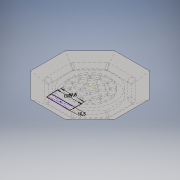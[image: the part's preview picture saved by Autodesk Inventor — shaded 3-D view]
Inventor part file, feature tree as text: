
AUTODESK INVENTOR PART (.ipt)
format: ipt  version: 2016 SP2 (Build 200236200, 236)  size: 281,088 bytes
history: native  units: mm
features: sketch x7, extrude x4, projected_geometry x2, sweep x1
ambient origin geometry x8: Origin, YZ Plane, XZ Plane, XY Plane, X Axis, Y Axis, Z Axis, Center Point
bodies: Body1 (feature_tree)
feature tree (14):
  sweep  "Sweeping2"
  extrude  "Extrusion1"  Depth=8.75mm
  extrude  "Extrusion2"  Depth=7.25mm
  extrude  "Extrusion3"  TaperAngle=0.0deg  [1 undecoded]
  extrude  "Extrusion4"  Depth=100.0mm
  sketch  "Skizze9"  dims[d25=5.0mm d26=0.0mm d27=14.0mm d28=11.0mm d29=14.0mm d30=11.0mm d31=6.0mm d32=50.0mm d34=360.0deg d36=14.0mm d37=11.0mm d38=5.0mm d39=120.0mm d41=360.0deg d43=3.0mm d44=0.0mm d45=2.0mm d46=0.0mm d47=50.0mm d48=47.8mm d49=10.5mm]
  sketch  "Skizze1"  dims[d4=10.5mm d10=50.0mm]
  sketch  "Skizze3"  dims[d11=100.0mm d12=8.75mm]
  sketch  "Skizze4"  dims[d13=8.75mm d14=7.25mm]
  projected_geometry  "Projizierte Kontur1"
  sketch  "Skizze5"  dims[d16=0.0mm d19=0.0mm d20=0.0mm]
  sketch  "Skizze7"  dims[d21=8.75mm d22=100.0mm]
  sketch  "Skizze8"  dims[d23=15.5mm d24=0.0mm]
  projected_geometry  "Projizierte Kontur2"
note: 1 required parameter value undecoded (feature->parameter linkage not recoverable at this tier; creation-order binding heuristic only, values carry confidence <= 0.55)
